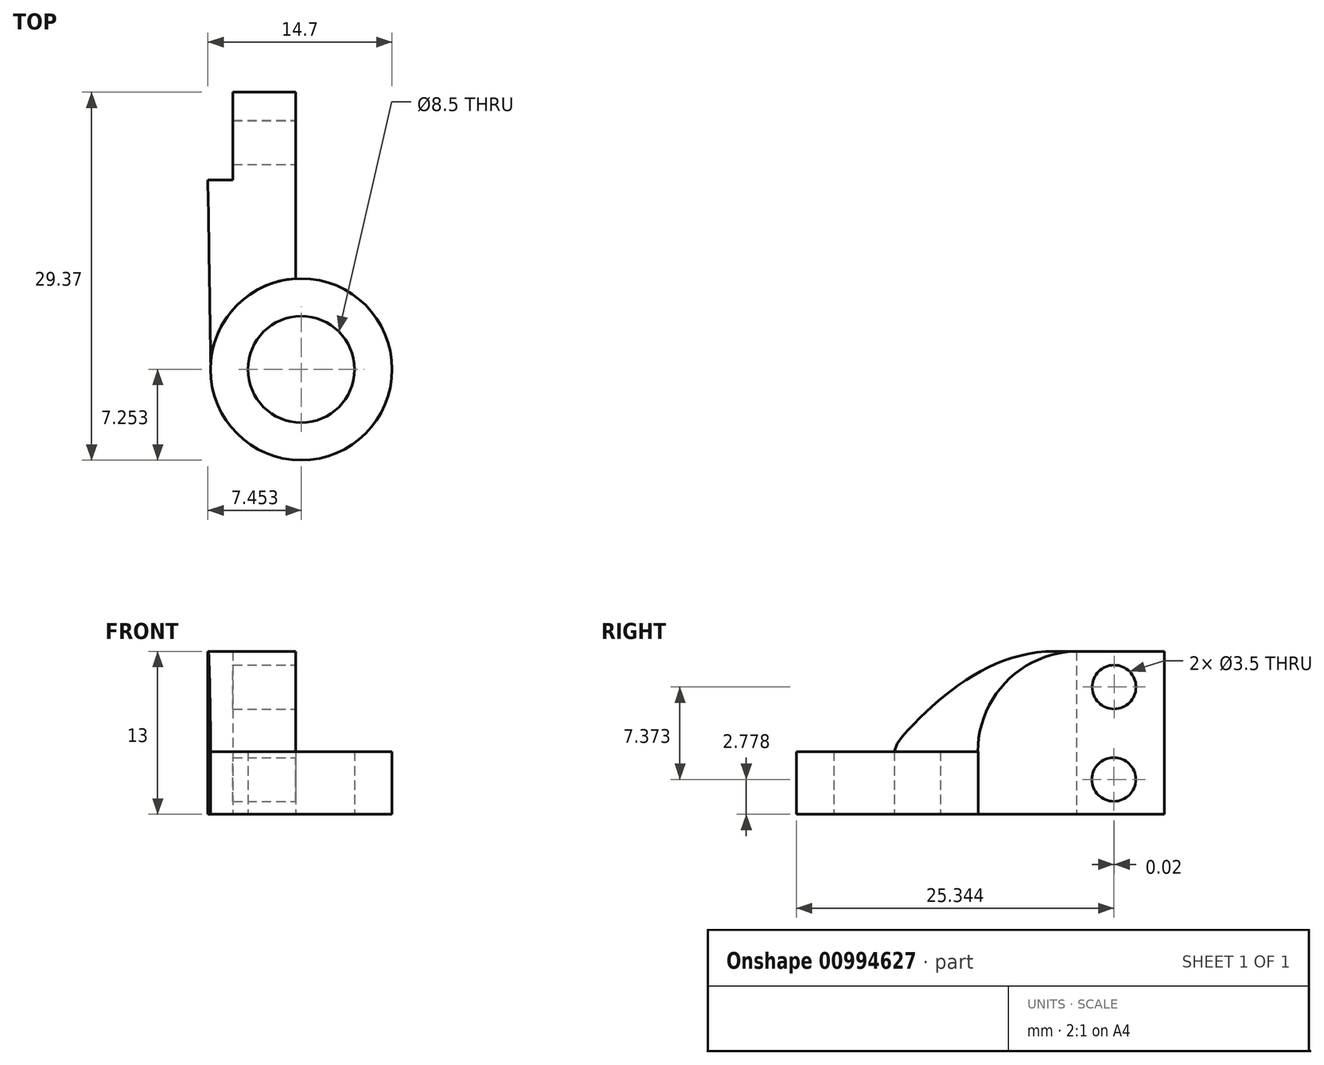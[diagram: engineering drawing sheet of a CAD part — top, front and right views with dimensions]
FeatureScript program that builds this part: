
annotation { "Feature Type Name" : "Feature", "Feature Type Description" : "" }
export const myFeature = defineFeature(function(context is Context, id is Id, definition is map)
    precondition{}
    {
        {
            var Q0;
            Q0=qCreatedBy(makeId("Top.planeOp"),FACE);
            var sketch = newSketch(context, id + "F0", { "sketchPlane" : qUnion([Q0])});
            skCircle(sketch, "E0", {"center": v(-0.1, -6.53) * mm, "radius": 7.25 * mm});
            skCircle(sketch, "E1", {"center": v(-0.1, -6.53) * mm, "radius": 4.25 * mm});
            skLineSegment(sketch, "E2.bottom", {"start": v(-5.56, 15.59) * mm, "end": v(-0.56, 15.59) * mm});
            skLineSegment(sketch, "E2.right", {"start": v(-0.56, 15.59) * mm, "end": v(-0.56, 0.7) * mm});
            skLineSegment(sketch, "E3", {"start": v(-7.34, -5.97) * mm, "end": v(-7.56, 8.59) * mm});
            skLineSegment(sketch, "E4", {"start": v(-7.56, 8.59) * mm, "end": v(-5.56, 8.59) * mm});
            skLineSegment(sketch, "E5", {"start": v(-5.56, 15.59) * mm, "end": v(-5.56, 8.59) * mm});
            skSolve(sketch);
        }
        {
            var Q0;
            Q0=makeQuery(id+"F0.imprint","IMPRINT",FACE,{"disambiguationData":[TD([[makeQuery(id+"F0.imprint","IMPRINT",EDGE,{"derivedFrom":sQuery(id+"F0.wireOp",EDGE,"E2.left")}),-1.0]])]});
            var Q1;
            {var subQ0=sQuery(id+"F0.wireOp",EDGE,"E2.top");Q1=makeQuery(id+"F0.imprint","IMPRINT",FACE,{"disambiguationData":[TD([[makeQuery(id+"F0.imprint","IMPRINT",EDGE,{"derivedFrom":subQ0}),-1.0]])]});}
            var Q2;
            Q2=makeQuery(id+"F0.imprint","IMPRINT",FACE,{"disambiguationData":[TD([[makeQuery(id+"F0.imprint","IMPRINT",EDGE,{"derivedFrom":sQuery(id+"F0.wireOp",EDGE,"E2.bottom")}),-1.0]])]});
            extrude(context, id + "F1", {"entities" : qUnion([Q0, Q1, Q2]), "depth" : 13 * mm, "offsetDistance" : 25 * mm});
        }
        {
            var Q0;
            Q0=qCreatedBy(makeId("Right.planeOp"),FACE);
            var sketch = newSketch(context, id + "F2", { "sketchPlane" : qUnion([Q0])});
            skCircle(sketch, "E6", {"center": v(11.58, 10.15) * mm, "radius": 1.75 * mm});
            skCircle(sketch, "E7", {"center": v(11.56, 2.78) * mm, "radius": 1.75 * mm});
            skSolve(sketch);
        }
        {
            var Q0;
            Q0=makeQuery(id+"F2.imprint","IMPRINT",FACE,{"disambiguationData":[TD([[makeQuery(id+"F2.imprint","IMPRINT",EDGE,{"derivedFrom":sQuery(id+"F2.wireOp",EDGE,"E6")}),1.0]])]});
            var Q1;
            Q1=makeQuery(id+"F2.imprint","IMPRINT",FACE,{"disambiguationData":[TD([[makeQuery(id+"F2.imprint","IMPRINT",EDGE,{"derivedFrom":sQuery(id+"F2.wireOp",EDGE,"E7")}),1.0]])]});
            var Q2;
            Q2=makeQuery(id+"F1.opExtrude","SWEPT_FACE",FACE,{"disambiguationData":[OSD([sQuery(id+"F0.wireOp",EDGE,"E5")])]});
            extrude(context, id + "F3", {"entities" : qUnion([Q0, Q1]), "operationType" : NewBodyOperationType.REMOVE, "endBound" : BoundingType.UP_TO_SURFACE, "oppositeDirection" : true, "depth" : 25 * mm, "endBoundEntityFace" : qUnion([Q2]), "offsetDistance" : 25 * mm});
        }
        {
            var Q0;
            Q0=makeQuery(id+"F0.imprint","IMPRINT",FACE,{"disambiguationData":[TD([[makeQuery(id+"F0.imprint","IMPRINT",EDGE,{"derivedFrom":sQuery(id+"F0.wireOp",EDGE,"E1")}),-1.0]])]});
            extrude(context, id + "F4", {"entities" : qUnion([Q0]), "depth" : 5 * mm, "offsetDistance" : 25 * mm});
        }
        {
            var Q0;
            Q0=makeQuery(id+"F1.opExtrude","CAP_EDGE",EDGE,{"disambiguationData":[OSD([sQuery(id+"F0.wireOp",EDGE,"E0")])],"isStart":false});
            fillet(context, id + "F5", {"entities" : qUnion([Q0]), "radius" : 8 * mm, "tangentPropagation" : true, "allowEdgeOverflow" : false});
        }
    });
